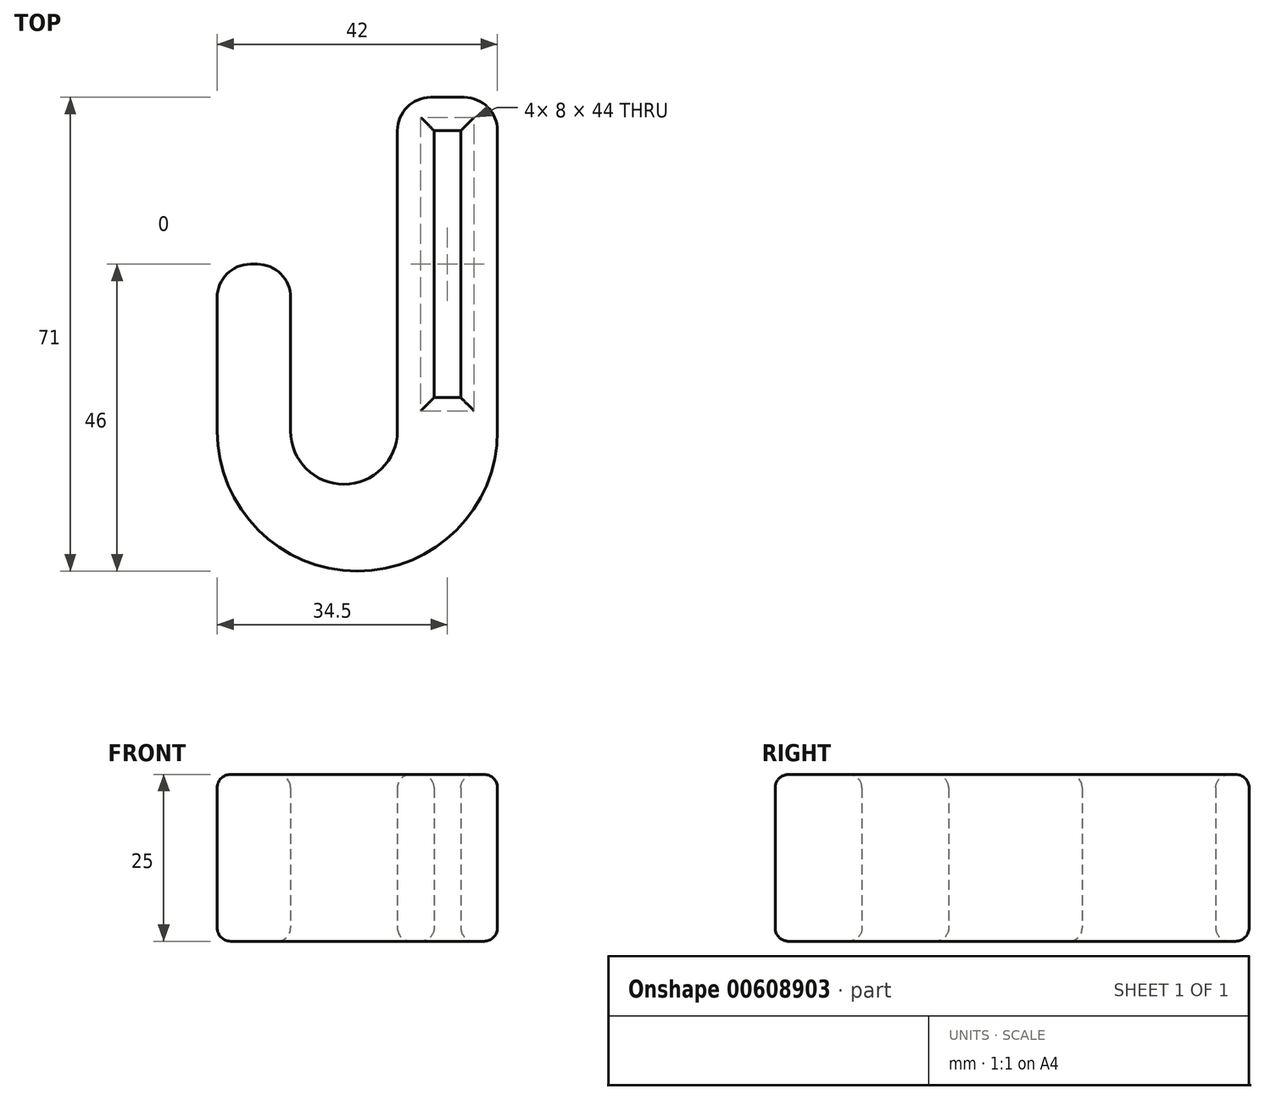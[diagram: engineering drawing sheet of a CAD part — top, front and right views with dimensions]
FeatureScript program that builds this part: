
annotation { "Feature Type Name" : "Feature", "Feature Type Description" : "" }
export const myFeature = defineFeature(function(context is Context, id is Id, definition is map)
    precondition{}
    {
        {
            var Q0;
            Q0=qCreatedBy(makeId("Top.planeOp"),FACE);
            var sketch = newSketch(context, id + "F0", { "sketchPlane" : qUnion([Q0])});
            skLineSegment(sketch, "E0.bottom", {"start": v(2, -20) * mm, "end": v(-2, -20) * mm});
            skLineSegment(sketch, "E0.top", {"start": v(2, 20) * mm, "end": v(-2, 20) * mm});
            skLineSegment(sketch, "E0.left", {"start": v(2, -20) * mm, "end": v(2, 20) * mm});
            skLineSegment(sketch, "E0.right", {"start": v(-2, -20) * mm, "end": v(-2, 20) * mm});
            skPoint(sketch, "E0.middle", {"position": v(0, 0) * mm});
            skLineSegment(sketch, "E1.top", {"start": v(7.5, 25) * mm, "end": v(-7.5, 25) * mm});
            skLineSegment(sketch, "E1.left", {"start": v(7.5, -25) * mm, "end": v(7.5, 25) * mm});
            skLineSegment(sketch, "E1.right", {"start": v(-7.5, -25) * mm, "end": v(-7.5, 25) * mm});
            skArc(sketch, "E2", {"start": v(-7.5, -25) * mm, "mid": v(-15.5, -33) * mm, "end": v(-23.5, -25) * mm});
            skArc(sketch, "E3", {"start": v(7.5, -25) * mm, "mid": v(-13.5, -46) * mm, "end": v(-34.5, -25) * mm});
            skLineSegment(sketch, "E4.top", {"start": v(-23.5, 0) * mm, "end": v(-34.5, 0) * mm});
            skLineSegment(sketch, "E4.left", {"start": v(-23.5, -25) * mm, "end": v(-23.5, 0) * mm});
            skLineSegment(sketch, "E4.right", {"start": v(-34.5, -25) * mm, "end": v(-34.5, 0) * mm});
            skSolve(sketch);
        }
        {
            var Q0;
            Q0 = qSketchRegion(id + "F0", true);
            extrude(context, id + "F1", {"entities" : qUnion([Q0]), "depth" : 25 * mm, "offsetDistance" : 25 * mm});
        }
        {
            var Q0;
            Q0=makeQuery(id+"F1.opExtrude","SWEPT_EDGE",EDGE,{"disambiguationData":[OSD([sQuery(id+"F0.wireOp",EDGE,"E1.top"),sQuery(id+"F0.wireOp",EDGE,"E1.right")])]});
            var Q1;
            Q1=makeQuery(id+"F1.opExtrude","SWEPT_EDGE",EDGE,{"disambiguationData":[OSD([sQuery(id+"F0.wireOp",EDGE,"E1.top"),sQuery(id+"F0.wireOp",EDGE,"E1.left")])]});
            var Q2;
            Q2=makeQuery(id+"F1.opExtrude","SWEPT_EDGE",EDGE,{"disambiguationData":[OSD([sQuery(id+"F0.wireOp",EDGE,"E4.top"),sQuery(id+"F0.wireOp",EDGE,"E4.left")])]});
            var Q3;
            Q3=makeQuery(id+"F1.opExtrude","SWEPT_EDGE",EDGE,{"disambiguationData":[OSD([sQuery(id+"F0.wireOp",EDGE,"E4.top"),sQuery(id+"F0.wireOp",EDGE,"E4.right")])]});
            fillet(context, id + "F2", {"entities" : qUnion([Q0, Q1, Q2, Q3]), "radius" : 5 * mm, "tangentPropagation" : true, "allowEdgeOverflow" : false});
        }
        {
            var Q0;
            Q0=makeQuery(id+"F1.opExtrude","CAP_FACE",FACE,{"disambiguationData":[OSD([sQuery(id+"F0.wireOp",EDGE,"E0.bottom"),sQuery(id+"F0.wireOp",EDGE,"E0.top"),sQuery(id+"F0.wireOp",EDGE,"E0.left"),sQuery(id+"F0.wireOp",EDGE,"E0.right"),sQuery(id+"F0.wireOp",EDGE,"E1.top"),sQuery(id+"F0.wireOp",EDGE,"E1.left"),sQuery(id+"F0.wireOp",EDGE,"E1.right"),sQuery(id+"F0.wireOp",EDGE,"E2"),sQuery(id+"F0.wireOp",EDGE,"E3"),sQuery(id+"F0.wireOp",EDGE,"E4.top"),sQuery(id+"F0.wireOp",EDGE,"E4.left"),sQuery(id+"F0.wireOp",EDGE,"E4.right")])],"isStart":false});
            var Q1;
            Q1=makeQuery(id+"F1.opExtrude","CAP_FACE",FACE,{"disambiguationData":[OSD([sQuery(id+"F0.wireOp",EDGE,"E0.bottom"),sQuery(id+"F0.wireOp",EDGE,"E0.top"),sQuery(id+"F0.wireOp",EDGE,"E0.left"),sQuery(id+"F0.wireOp",EDGE,"E0.right"),sQuery(id+"F0.wireOp",EDGE,"E1.top"),sQuery(id+"F0.wireOp",EDGE,"E1.left"),sQuery(id+"F0.wireOp",EDGE,"E1.right"),sQuery(id+"F0.wireOp",EDGE,"E2"),sQuery(id+"F0.wireOp",EDGE,"E3"),sQuery(id+"F0.wireOp",EDGE,"E4.top"),sQuery(id+"F0.wireOp",EDGE,"E4.left"),sQuery(id+"F0.wireOp",EDGE,"E4.right")])],"isStart":true});
            fillet(context, id + "F3", {"entities" : qUnion([Q0, Q1]), "radius" : 2 * mm, "tangentPropagation" : true, "allowEdgeOverflow" : false});
        }
    });
